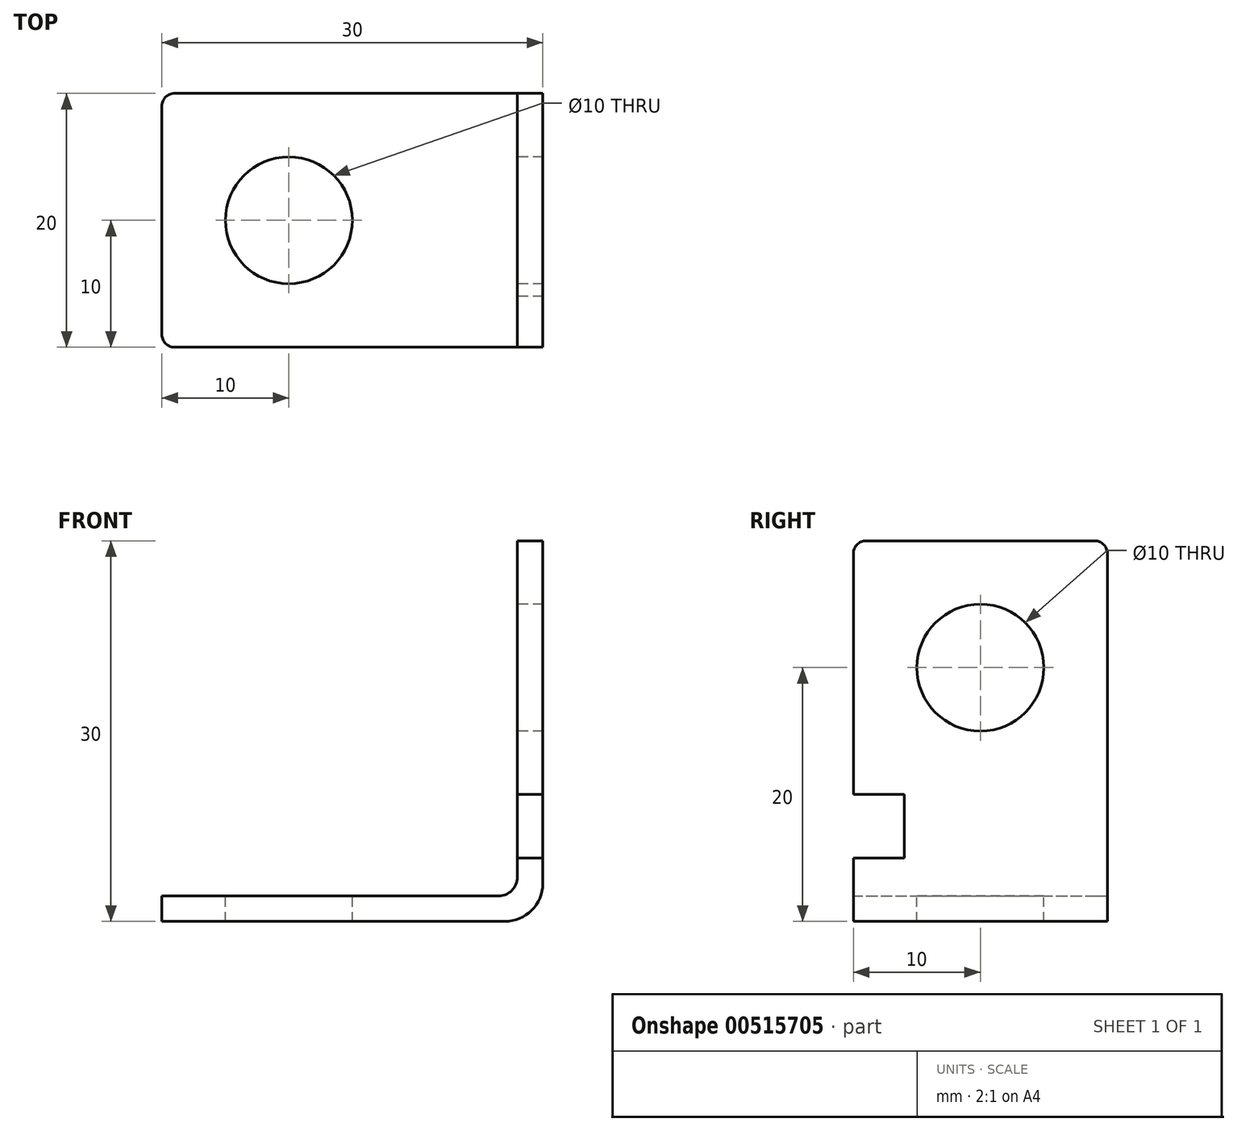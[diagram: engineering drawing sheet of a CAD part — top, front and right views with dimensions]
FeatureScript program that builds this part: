
annotation { "Feature Type Name" : "Feature", "Feature Type Description" : "" }
export const myFeature = defineFeature(function(context is Context, id is Id, definition is map)
    precondition{}
    {
        {
            var Q0;
            Q0=qCreatedBy(makeId("Front.planeOp"),FACE);
            var sketch = newSketch(context, id + "F0", { "sketchPlane" : qUnion([Q0])});
            skLineSegment(sketch, "E0", {"start": v(0, 0) * mm, "end": v(27, 0) * mm});
            skLineSegment(sketch, "E1", {"start": v(30, 3) * mm, "end": v(30, 30) * mm});
            skLineSegment(sketch, "E2", {"start": v(30, 30) * mm, "end": v(28, 30) * mm});
            skLineSegment(sketch, "E3", {"start": v(28, 30) * mm, "end": v(28, 3.5) * mm});
            skLineSegment(sketch, "E4", {"start": v(26.5, 2) * mm, "end": v(0, 2) * mm});
            skLineSegment(sketch, "E5", {"start": v(0, 2) * mm, "end": v(0, 0) * mm});
            skPoint(sketch, "E6.visualSharp", {"position": v(30, 0) * mm});
            skArc(sketch, "E6.filletArc", {"start": v(27, 0) * mm, "mid": v(29.12, 0.88) * mm, "end": v(30, 3) * mm});
            skPoint(sketch, "E7.visualSharp", {"position": v(28, 2) * mm});
            skArc(sketch, "E7.filletArc", {"start": v(26.5, 2) * mm, "mid": v(27.56, 2.44) * mm, "end": v(28, 3.5) * mm});
            skSolve(sketch);
        }
        {
            var Q0;
            Q0 = qSketchRegion(id + "F0", true);
            extrude(context, id + "F1", {"entities" : qUnion([Q0]), "depth" : 20 * mm, "offsetDistance" : 25 * mm});
        }
        {
            var Q0;
            Q0=makeQuery(id+"F1.opExtrude","CAP_EDGE",EDGE,{"disambiguationData":[OSD([sQuery(id+"F0.wireOp",EDGE,"E2")])],"isStart":false});
            var Q1;
            Q1=makeQuery(id+"F1.opExtrude","CAP_EDGE",EDGE,{"disambiguationData":[OSD([sQuery(id+"F0.wireOp",EDGE,"E2")])],"isStart":true});
            var Q2;
            Q2=makeQuery(id+"F1.opExtrude","CAP_EDGE",EDGE,{"disambiguationData":[OSD([sQuery(id+"F0.wireOp",EDGE,"E5")])],"isStart":false});
            var Q3;
            Q3=makeQuery(id+"F1.opExtrude","CAP_EDGE",EDGE,{"disambiguationData":[OSD([sQuery(id+"F0.wireOp",EDGE,"E5")])],"isStart":true});
            fillet(context, id + "F2", {"entities" : qUnion([Q0, Q1, Q2, Q3]), "radius" : 1 * mm, "tangentPropagation" : true, "allowEdgeOverflow" : false});
        }
        {
            var Q0;
            Q0=makeQuery(id+"F1.opExtrude","SWEPT_FACE",FACE,{"disambiguationData":[OSD([sQuery(id+"F0.wireOp",EDGE,"E3")])]});
            var sketch = newSketch(context, id + "F3", { "sketchPlane" : qUnion([Q0])});
            skCircle(sketch, "E8", {"center": v(10, 20) * mm, "radius": 5 * mm});
            skLineSegment(sketch, "E9", {"start": v(21, 10) * mm, "end": v(16, 10) * mm});
            skLineSegment(sketch, "E10", {"start": v(16, 10) * mm, "end": v(16, 5) * mm});
            skLineSegment(sketch, "E11", {"start": v(16, 5) * mm, "end": v(21, 5) * mm});
            skLineSegment(sketch, "E12", {"start": v(21, 10) * mm, "end": v(21, 5) * mm});
            skSolve(sketch);
        }
        {
            var Q0;
            Q0 = qSketchRegion(id + "F3", true);
            extrude(context, id + "F4", {"entities" : qUnion([Q0]), "operationType" : NewBodyOperationType.REMOVE, "endBound" : BoundingType.THROUGH_ALL, "oppositeDirection" : true, "depth" : 25 * mm, "offsetDistance" : 25 * mm});
        }
        {
            var Q0;
            Q0=makeQuery(id+"F1.opExtrude","SWEPT_FACE",FACE,{"disambiguationData":[OSD([sQuery(id+"F0.wireOp",EDGE,"E4")])]});
            var sketch = newSketch(context, id + "F5", { "sketchPlane" : qUnion([Q0])});
            skCircle(sketch, "E13", {"center": v(10, -10) * mm, "radius": 5 * mm});
            skSolve(sketch);
        }
        {
            var Q0;
            Q0 = qSketchRegion(id + "F5", true);
            extrude(context, id + "F6", {"entities" : qUnion([Q0]), "operationType" : NewBodyOperationType.REMOVE, "endBound" : BoundingType.THROUGH_ALL, "oppositeDirection" : true, "depth" : 25 * mm, "offsetDistance" : 25 * mm});
        }
    });
